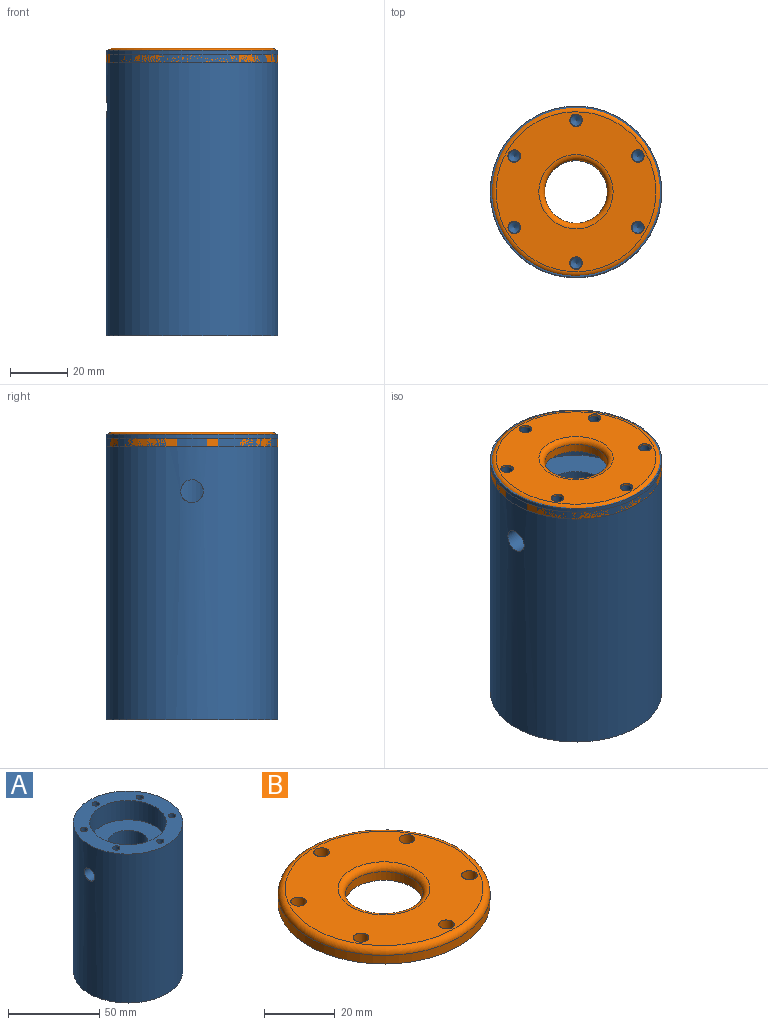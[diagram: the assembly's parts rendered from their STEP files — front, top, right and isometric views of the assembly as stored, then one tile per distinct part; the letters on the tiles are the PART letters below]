
ASSEMBLY  parts=2 mates=1
PART A: 33 faces, bbox 60x60x100 mm
  f0: cylinder r=11mm len=74mm, axis (0,0,-1), area 5063.5mm2, adj f5,f7,f8
  f1: cylinder r=30mm len=100mm, axis (0,0,-1), area 18798.9mm2, adj f2,f3,f8
  f2: plane 60x60mm, normal (0,0,1), area 1366.6mm2, adj f1,f4,f10,f12,f14,f16,f18,f20
  f3: plane 60x60mm, normal (0,0,-1), area 1366.6mm2, adj f1,f6,f22,f24,f26,f28,f30,f32
  f4: cylinder r=21mm len=42mm, axis (0,0,1), area 1715.3mm2, adj f2,f5
  f5: plane 42x42mm, normal (0,0,1), area 1005.3mm2, adj f0,f4
  f6: cylinder r=21mm len=42mm, axis (0,0,-1), area 1715.3mm2, adj f3,f7
  f7: plane 42x42mm, normal (0,0,-1), area 1005.3mm2, adj f0,f6
  f8: cylinder r=4mm len=19.75mm, axis (1,0,0), area 483.6mm2, adj f0,f1
  f9: cone r=0mm half-angle=59deg, axis (0,0,1), area 14.7mm2, adj f10
  f10: cylinder r=2mm len=30mm, axis (0,0,1), area 377mm2, adj f2,f9
  f11: cone r=0mm half-angle=59deg, axis (0,0,1), area 14.7mm2, adj f12
  f12: cylinder r=2mm len=30mm, axis (0,0,1), area 377mm2, adj f2,f11
  f13: cone r=0mm half-angle=59deg, axis (0,0,1), area 14.7mm2, adj f14
  f14: cylinder r=2mm len=30mm, axis (0,0,1), area 377mm2, adj f2,f13
  f15: cone r=0mm half-angle=59deg, axis (0,0,1), area 14.7mm2, adj f16
  f16: cylinder r=2mm len=30mm, axis (0,0,1), area 377mm2, adj f2,f15
  f17: cone r=0mm half-angle=59deg, axis (0,0,1), area 14.7mm2, adj f18
  f18: cylinder r=2mm len=30mm, axis (0,0,1), area 377mm2, adj f2,f17
  f19: cone r=0mm half-angle=59deg, axis (0,0,1), area 14.7mm2, adj f20
  f20: cylinder r=2mm len=30mm, axis (0,0,1), area 377mm2, adj f2,f19
  f21: cone r=0mm half-angle=59deg, axis (0,0,-1), area 14.7mm2, adj f22
  f22: cylinder r=2mm len=30mm, axis (0,0,-1), area 377mm2, adj f3,f21
  f23: cone r=0mm half-angle=59deg, axis (0,0,-1), area 14.7mm2, adj f24
  f24: cylinder r=2mm len=30mm, axis (0,0,-1), area 377mm2, adj f3,f23
  f25: cone r=0mm half-angle=59deg, axis (0,0,-1), area 14.7mm2, adj f26
  f26: cylinder r=2mm len=30mm, axis (0,0,-1), area 377mm2, adj f3,f25
  f27: cone r=0mm half-angle=59deg, axis (0,0,-1), area 14.7mm2, adj f28
  f28: cylinder r=2mm len=30mm, axis (0,0,-1), area 377mm2, adj f3,f27
  f29: cone r=0mm half-angle=59deg, axis (0,0,-1), area 14.7mm2, adj f30
  f30: cylinder r=2mm len=30mm, axis (0,0,-1), area 377mm2, adj f3,f29
  f31: cone r=0mm half-angle=59deg, axis (0,0,-1), area 14.7mm2, adj f32
  f32: cylinder r=2mm len=30mm, axis (0,0,-1), area 377mm2, adj f3,f31
PART B: 12 faces, bbox 64.9x64.9x5 mm
  f0: cylinder r=11mm len=22mm, axis (0,0,-1), area 207.3mm2, adj f9,f11
  f1: cylinder r=2.2mm len=5mm, axis (0,0,-1), area 69.1mm2, adj f8,f9
  f2: cylinder r=2.2mm len=5mm, axis (0,0,-1), area 69.1mm2, adj f8,f9
  f3: cylinder r=2.2mm len=5mm, axis (0,0,-1), area 69.1mm2, adj f8,f9
  f4: cylinder r=2.2mm len=5mm, axis (0,0,-1), area 69.1mm2, adj f8,f9
  f5: cylinder r=2.2mm len=5mm, axis (0,0,-1), area 69.1mm2, adj f8,f9
  f6: cylinder r=2.2mm len=5mm, axis (0,0,-1), area 69.1mm2, adj f8,f9
  f7: cylinder r=30mm len=60mm, axis (0,0,-1), area 565.5mm2, adj f9,f10
  f8: plane 56x56mm, normal (0,0,1), area 1840.8mm2, adj f1,f2,f3,f4,f5,f6,f10,f11
  f9: plane 60x60mm, normal (0,0,-1), area 2356.1mm2, adj f0,f1,f2,f3,f4,f5,f6,f7
  f10: torus R=28mm, axis (0,0,1), area 577.8mm2, adj f7,f8
  f11: torus R=13mm, axis (0,0,1), area 231.5mm2, adj f0,f8
PLACE A t=(-44.37,51.42,-6.44)mm
PLACE B t=(-44.37,51.42,89.14)mm
MATE fastened B.f7 <-> A.f1  axis (0,0,1) through (-44.37,51.42,93.56)mm
